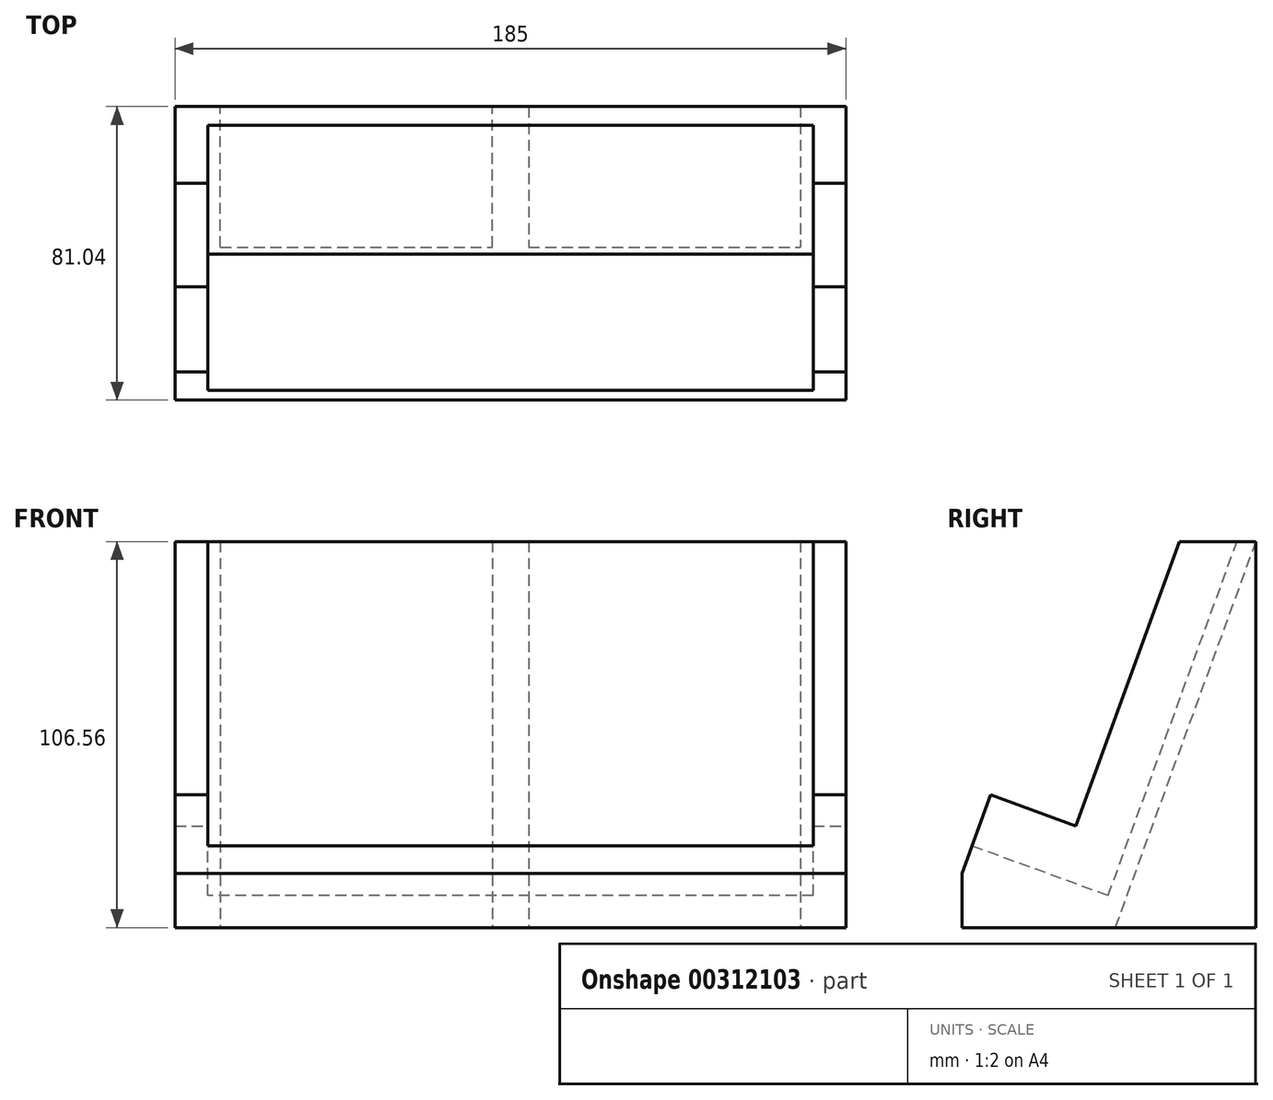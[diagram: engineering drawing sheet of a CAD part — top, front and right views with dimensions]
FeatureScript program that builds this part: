
annotation { "Feature Type Name" : "Feature", "Feature Type Description" : "" }
export const myFeature = defineFeature(function(context is Context, id is Id, definition is map)
    precondition{}
    {
        {
            var Q0;
            Q0=qCreatedBy(makeId("Right.planeOp"),FACE);
            var sketch = newSketch(context, id + "F0", { "sketchPlane" : qUnion([Q0])});
            skLineSegment(sketch, "E0", {"start": v(0, 0) * mm, "end": v(41.04, 0) * mm});
            skLineSegment(sketch, "E1", {"start": v(0, 0) * mm, "end": v(0, 77.2) * mm, "construction": true});
            skLineSegment(sketch, "E2", {"start": v(41.04, 0) * mm, "end": v(41.04, 112.76) * mm});
            skLineSegment(sketch, "E3", {"start": v(0, 0) * mm, "end": v(41.04, 112.76) * mm});
            skLineSegment(sketch, "E4.bottom", {"start": v(41.04, 0) * mm, "end": v(81.04, 0) * mm});
            skLineSegment(sketch, "E4.top", {"start": v(41.04, 112.76) * mm, "end": v(81.04, 112.76) * mm});
            skLineSegment(sketch, "E4.right", {"start": v(81.04, 0) * mm, "end": v(81.04, 112.76) * mm});
            skLineSegment(sketch, "E5.bottom", {"start": v(0, 0) * mm, "end": v(81.04, 0) * mm});
            skLineSegment(sketch, "E5.top", {"start": v(0, -15) * mm, "end": v(81.04, -15) * mm});
            skLineSegment(sketch, "E5.left", {"start": v(0, 0) * mm, "end": v(0, -15) * mm});
            skLineSegment(sketch, "E5.right", {"start": v(81.04, 0) * mm, "end": v(81.04, -15) * mm});
            skSolve(sketch);
        }
        {
            var Q0;
            Q0=qSketchRegion(id+"F0",true);
            extrude(context, id + "F1", {"entities" : qUnion([Q0]), "endBound" : BoundingType.SYMMETRIC, "depth" : (55 * 3 + 20) * mm});
        }
        {
            var Q0;
            Q0=makeQuery(id+"F1.opExtrude","SWEPT_FACE",FACE,{"disambiguationData":[OSD([sQuery(id+"F0.wireOp",EDGE,"E3")])]});
            var sketch = newSketch(context, id + "F2", { "sketchPlane" : qUnion([Q0])});
            skLineSegment(sketch, "E6.0.0", {"start": v(-92.5, 120) * mm, "end": v(-92.5, 0) * mm, "construction": true});
            skLineSegment(sketch, "E6.0.1", {"start": v(-92.5, 0) * mm, "end": v(92.5, 0) * mm, "construction": true});
            skLineSegment(sketch, "E6.0.2", {"start": v(92.5, 0) * mm, "end": v(92.5, 120) * mm, "construction": true});
            skLineSegment(sketch, "E6.0.3", {"start": v(92.5, 120) * mm, "end": v(-92.5, 120) * mm, "construction": true});
            skLineSegment(sketch, "E7", {"start": v(-92.5, 120) * mm, "end": v(92.5, 0) * mm, "construction": true});
            skLineSegment(sketch, "E8", {"start": v(92.5, 120) * mm, "end": v(-92.5, 0) * mm, "construction": true});
            skPoint(sketch, "E9", {"position": v(0, 60) * mm});
            skLineSegment(sketch, "E10.bottom", {"start": v(83.5, 8) * mm, "end": v(-83.5, 8) * mm});
            skLineSegment(sketch, "E10.top", {"start": v(83.5, 112) * mm, "end": v(-83.5, 112) * mm});
            skLineSegment(sketch, "E10.left", {"start": v(83.5, 8) * mm, "end": v(83.5, 112) * mm});
            skLineSegment(sketch, "E10.right", {"start": v(-83.5, 8) * mm, "end": v(-83.5, 112) * mm});
            skSolve(sketch);
        }
        {
            var Q0;
            Q0=makeQuery(id+"F2.imprint","IMPRINT",FACE,{"disambiguationData":[TD([[makeQuery(id+"F2.imprint","IMPRINT",EDGE,{"derivedFrom":sQuery(id+"F2.wireOp",EDGE,"E10.bottom")}),-1.0]])]});
            extrude(context, id + "F3", {"entities" : qUnion([Q0]), "operationType" : NewBodyOperationType.REMOVE, "oppositeDirection" : true, "depth" : 40 * mm});
        }
        {
            var Q0;
            Q0=makeQuery(id+"F1.opExtrude","CAP_FACE",FACE,{"disambiguationData":[OSD([sQuery(id+"F0.wireOp",EDGE,"E3"),sQuery(id+"F0.wireOp",EDGE,"E4.top"),sQuery(id+"F0.wireOp",EDGE,"E4.right"),sQuery(id+"F0.wireOp",EDGE,"E5.top"),sQuery(id+"F0.wireOp",EDGE,"E5.left"),sQuery(id+"F0.wireOp",EDGE,"E5.right")])],"isStart":false});
            var sketch = newSketch(context, id + "F4", { "sketchPlane" : qUnion([Q0])});
            skLineSegment(sketch, "E11.0", {"start": v(75.9, 91.56) * mm, "end": v(38.3, 105.25) * mm, "construction": true});
            skLineSegment(sketch, "E12.0", {"start": v(40.32, -6.16) * mm, "end": v(75.9, 91.56) * mm, "construction": true});
            skLineSegment(sketch, "E13.0", {"start": v(41.04, 112.76) * mm, "end": v(81.04, 112.76) * mm, "construction": true});
            skLineSegment(sketch, "E14.bottom", {"start": v(100.15, 112.76) * mm, "end": v(33, 112.76) * mm});
            skLineSegment(sketch, "E14.top", {"start": v(100.15, 91.56) * mm, "end": v(33, 91.56) * mm});
            skLineSegment(sketch, "E14.left", {"start": v(100.15, 112.76) * mm, "end": v(100.15, 91.56) * mm});
            skLineSegment(sketch, "E14.right", {"start": v(33, 112.76) * mm, "end": v(33, 91.56) * mm});
            skSolve(sketch);
        }
        {
            var Q0;
            {var subQ3=sQuery(id+"F4.wireOp",EDGE,"E14.left");Q0=makeQuery(id+"F4.imprint","IMPRINT",FACE,{"disambiguationData":[TD([[makeQuery(id+"F4.imprint","IMPRINT",EDGE,{"derivedFrom":subQ3}),-1.0]])]});}
            var Q1;
            {var subQ0=sQuery(id+"F4.wireOp",EDGE,"E14.bottom");var subQ1=makeQuery(id+"F1.opExtrude","CAP_EDGE",EDGE,{"disambiguationData":[OSD([sQuery(id+"F0.wireOp",EDGE,"E3")])],"isStart":false});var subQ2=makeQuery(id+"F4.imprint","INTERSECT",VERTEX,{"derivedFrom":[subQ1,subQ0]});Q1=makeQuery(id+"F4.imprint","IMPRINT",FACE,{"disambiguationData":[TD([[makeQuery(id+"F4.imprint","IMPRINT",EDGE,{"disambiguationData":[TD([[subQ2,1.0]])],"derivedFrom":subQ1}),-1.0]])]});}
            var Q2;
            {var subQ3=sQuery(id+"F4.wireOp",EDGE,"E14.right");Q2=makeQuery(id+"F4.imprint","IMPRINT",FACE,{"disambiguationData":[TD([[makeQuery(id+"F4.imprint","IMPRINT",EDGE,{"derivedFrom":subQ3}),1.0]])]});}
            extrude(context, id + "F5", {"entities" : qUnion([Q0, Q1, Q2]), "operationType" : NewBodyOperationType.REMOVE, "oppositeDirection" : true, "depth" : 200 * mm});
        }
        {
            var Q0;
            Q0=makeQuery(id+"F1.opExtrude","CAP_FACE",FACE,{"disambiguationData":[OSD([sQuery(id+"F0.wireOp",EDGE,"E3"),sQuery(id+"F0.wireOp",EDGE,"E4.top"),sQuery(id+"F0.wireOp",EDGE,"E4.right"),sQuery(id+"F0.wireOp",EDGE,"E5.top"),sQuery(id+"F0.wireOp",EDGE,"E5.left"),sQuery(id+"F0.wireOp",EDGE,"E5.right")])],"isStart":false});
            var sketch = newSketch(context, id + "F6", { "sketchPlane" : qUnion([Q0])});
            skLineSegment(sketch, "E15.0", {"start": v(0, 0) * mm, "end": v(33.33, 91.56) * mm, "construction": true});
            skLineSegment(sketch, "E16.0", {"start": v(81.04, 91.56) * mm, "end": v(33.33, 91.56) * mm, "construction": true});
            skLineSegment(sketch, "E17.0", {"start": v(40.32, -6.16) * mm, "end": v(75.9, 91.56) * mm, "construction": true});
            skLineSegment(sketch, "E18.0", {"start": v(40.32, -6.16) * mm, "end": v(2.74, 7.52) * mm, "construction": true});
            skLineSegment(sketch, "E19", {"start": v(7.87, 21.61) * mm, "end": v(45.45, 7.93) * mm});
            skLineSegment(sketch, "E20", {"start": v(59.93, 91.56) * mm, "end": v(26.23, -1.03) * mm});
            skLineSegment(sketch, "E21", {"start": v(33.33, 91.56) * mm, "end": v(59.93, 91.56) * mm});
            skLineSegment(sketch, "E22", {"start": v(33.33, 91.56) * mm, "end": v(7.87, 21.61) * mm});
            skSolve(sketch);
        }
        {
            var Q0;
            {var subQ4=sQuery(id+"F6.wireOp",EDGE,"E21");Q0=makeQuery(id+"F6.imprint","IMPRINT",FACE,{"disambiguationData":[TD([[makeQuery(id+"F6.imprint","IMPRINT",EDGE,{"derivedFrom":subQ4}),1.0]])]});}
            extrude(context, id + "F7", {"entities" : qUnion([Q0]), "operationType" : NewBodyOperationType.REMOVE, "oppositeDirection" : true, "depth" : 200 * mm});
        }
        {
            var Q0;
            Q0=qCreatedBy(makeId("Right.planeOp"),FACE);
            var sketch = newSketch(context, id + "F8", { "sketchPlane" : qUnion([Q0])});
            skLineSegment(sketch, "E23.0", {"start": v(40.32, -6.16) * mm, "end": v(75.9, 91.56) * mm, "construction": true});
            skLineSegment(sketch, "E24.0", {"start": v(81.04, 91.56) * mm, "end": v(59.93, 91.56) * mm, "construction": true});
            skLineSegment(sketch, "E25.0", {"start": v(81.04, -15) * mm, "end": v(81.04, 91.56) * mm, "construction": true});
            skLineSegment(sketch, "E26.0", {"start": v(0, -15) * mm, "end": v(81.04, -15) * mm, "construction": true});
            skLineSegment(sketch, "E27", {"start": v(81.04, 91.56) * mm, "end": v(42.26, -15) * mm});
            skLineSegment(sketch, "E28", {"start": v(42.26, -15) * mm, "end": v(81.04, -15) * mm});
            skLineSegment(sketch, "E29", {"start": v(81.04, 91.56) * mm, "end": v(81.04, -15) * mm});
            skSolve(sketch);
        }
        {
            var Q0;
            Q0 = qSketchRegion(id + "F8", true);
            extrude(context, id + "F9", {"entities" : qUnion([Q0]), "operationType" : NewBodyOperationType.REMOVE, "endBound" : BoundingType.SYMMETRIC, "oppositeDirection" : true, "depth" : 160 * mm});
        }
        {
            var Q0;
            Q0 = qSketchRegion(id + "F8", true);
            extrude(context, id + "F10", {"entities" : qUnion([Q0]), "operationType" : NewBodyOperationType.ADD, "endBound" : BoundingType.SYMMETRIC, "depth" : 10 * mm});
        }
    });
